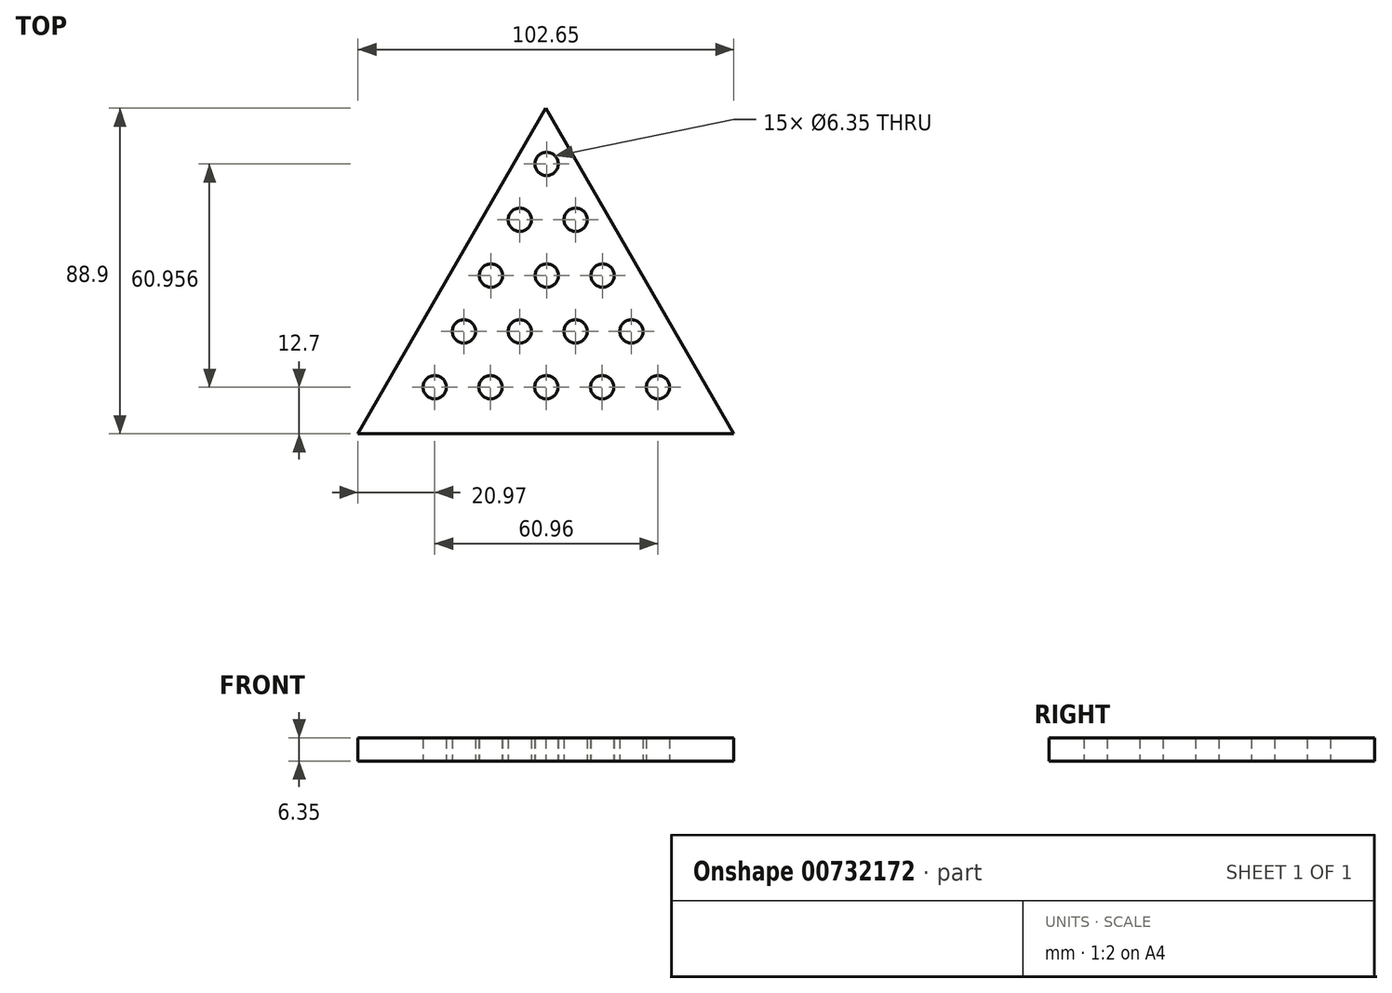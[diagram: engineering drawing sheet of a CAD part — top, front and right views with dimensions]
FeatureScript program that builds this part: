
annotation { "Feature Type Name" : "Feature", "Feature Type Description" : "" }
export const myFeature = defineFeature(function(context is Context, id is Id, definition is map)
    precondition{}
    {
        {
            var Q0;
            Q0=qCreatedBy(makeId("Top.planeOp"),FACE);
            var sketch = newSketch(context, id + "F0", { "sketchPlane" : qUnion([Q0])});
            skLineSegment(sketch, "E0.bottom", {"start": v(0, 0) * mm, "end": v(88.9, 0) * mm});
            skLineSegment(sketch, "E0.top", {"start": v(0, 88.9) * mm, "end": v(88.9, 88.9) * mm});
            skLineSegment(sketch, "E0.left", {"start": v(0, 0) * mm, "end": v(0, 88.9) * mm});
            skLineSegment(sketch, "E0.right", {"start": v(88.9, 0) * mm, "end": v(88.9, 88.9) * mm});
            skSolve(sketch);
        }
        {
            var Q0;
            Q0=makeQuery(id+"F0.imprint","IMPRINT",FACE,{"disambiguationData":[TD([[makeQuery(id+"F0.imprint","IMPRINT",EDGE,{"derivedFrom":sQuery(id+"F0.wireOp",EDGE,"E0.bottom")}),1.0]])]});
            var sketch = newSketch(context, id + "F1", { "sketchPlane" : qUnion([Q0])});
            skCircle(sketch, "E1", {"center": v(12.7, 12.7) * mm, "radius": 3.18 * mm});
            skCircle(sketch, "E2.1.0.0", {"center": v(27.94, 12.7) * mm, "radius": 3.18 * mm});
            skCircle(sketch, "E2.2.0.0", {"center": v(43.18, 12.7) * mm, "radius": 3.18 * mm});
            skCircle(sketch, "E2.3.0.0", {"center": v(58.42, 12.7) * mm, "radius": 3.18 * mm});
            skCircle(sketch, "E2.4.0.0", {"center": v(73.66, 12.7) * mm, "radius": 3.18 * mm});
            skLineSegment(sketch, "E2.direction1", {"start": v(12.7, 12.7) * mm, "end": v(27.94, 12.7) * mm, "construction": true});
            skSolve(sketch);
        }
        {
            var Q0;
            Q0=makeQuery(id+"F0.imprint","IMPRINT",FACE,{"disambiguationData":[TD([[makeQuery(id+"F0.imprint","IMPRINT",EDGE,{"derivedFrom":sQuery(id+"F0.wireOp",EDGE,"E0.bottom")}),1.0]])]});
            var sketch = newSketch(context, id + "F2", { "sketchPlane" : qUnion([Q0])});
            skCircle(sketch, "E3", {"center": v(20.67, 27.94) * mm, "radius": 3.18 * mm});
            skCircle(sketch, "E4.1.0.0", {"center": v(35.9, 27.94) * mm, "radius": 3.18 * mm});
            skCircle(sketch, "E4.2.0.0", {"center": v(51.15, 27.94) * mm, "radius": 3.18 * mm});
            skCircle(sketch, "E4.3.0.0", {"center": v(66.39, 27.94) * mm, "radius": 3.18 * mm});
            skLineSegment(sketch, "E4.direction1", {"start": v(20.67, 27.94) * mm, "end": v(35.9, 27.94) * mm, "construction": true});
            skSolve(sketch);
        }
        {
            var Q0;
            Q0=makeQuery(id+"F1.imprint","IMPRINT",FACE,{"disambiguationData":[TD([[makeQuery(id+"F1.imprint","IMPRINT",EDGE,{"derivedFrom":sQuery(id+"F1.wireOp",EDGE,"E1")}),-1.0]])]});
            var sketch = newSketch(context, id + "F3", { "sketchPlane" : qUnion([Q0])});
            skCircle(sketch, "E5", {"center": v(28.08, 43.18) * mm, "radius": 3.17 * mm});
            skCircle(sketch, "E6.1.0.0", {"center": v(43.32, 43.18) * mm, "radius": 3.17 * mm});
            skCircle(sketch, "E6.2.0.0", {"center": v(58.56, 43.18) * mm, "radius": 3.17 * mm});
            skLineSegment(sketch, "E6.direction1", {"start": v(28.08, 43.18) * mm, "end": v(43.32, 43.18) * mm, "construction": true});
            skSolve(sketch);
        }
        {
            var Q0;
            Q0=makeQuery(id+"F1.imprint","IMPRINT",FACE,{"disambiguationData":[TD([[makeQuery(id+"F1.imprint","IMPRINT",EDGE,{"derivedFrom":sQuery(id+"F1.wireOp",EDGE,"E1")}),-1.0]])]});
            var sketch = newSketch(context, id + "F4", { "sketchPlane" : qUnion([Q0])});
            skCircle(sketch, "E7", {"center": v(35.94, 58.42) * mm, "radius": 3.18 * mm});
            skCircle(sketch, "E8.1.0.0", {"center": v(51.18, 58.42) * mm, "radius": 3.18 * mm});
            skLineSegment(sketch, "E8.direction1", {"start": v(35.94, 58.42) * mm, "end": v(51.18, 58.42) * mm, "construction": true});
            skSolve(sketch);
        }
        {
            var Q0;
            Q0=makeQuery(id+"F2.imprint","IMPRINT",FACE,{"disambiguationData":[TD([[makeQuery(id+"F2.imprint","IMPRINT",EDGE,{"derivedFrom":sQuery(id+"F2.wireOp",EDGE,"E3")}),-1.0]])]});
            var sketch = newSketch(context, id + "F5", { "sketchPlane" : qUnion([Q0])});
            skCircle(sketch, "E9", {"center": v(43.23, 73.66) * mm, "radius": 3.17 * mm});
            skSolve(sketch);
        }
        {
            var Q0;
            Q0=makeQuery(id+"F1.imprint","IMPRINT",FACE,{"disambiguationData":[TD([[makeQuery(id+"F1.imprint","IMPRINT",EDGE,{"derivedFrom":sQuery(id+"F1.wireOp",EDGE,"E1")}),-1.0]])]});
            var sketch = newSketch(context, id + "F6", { "sketchPlane" : qUnion([Q0])});
            skCircle(sketch, "E10.cCircle", {"center": v(43.05, 29.63) * mm, "radius": 29.63 * mm, "construction": true});
            skLineSegment(sketch, "E10.0", {"start": v(94.38, 0) * mm, "end": v(-8.27, 0) * mm});
            skLineSegment(sketch, "E10.1", {"start": v(-8.27, 0) * mm, "end": v(43.05, 88.9) * mm});
            skLineSegment(sketch, "E10.2", {"start": v(43.05, 88.9) * mm, "end": v(94.38, 0) * mm});
            skPoint(sketch, "E10.0.midPoint", {"position": v(43.05, 0) * mm});
            skSolve(sketch);
        }
        {
            var Q0;
            Q0 = qSketchRegion(id + "F6", true);
            extrude(context, id + "F7", {"entities" : qUnion([Q0]), "depth" : 6.35 * mm, "offsetDistance" : 25.4 * mm});
        }
        {
            var Q0;
            Q0 = qSketchRegion(id + "F5", true);
            var Q1;
            Q1 = qSketchRegion(id + "F1", true);
            var Q2;
            Q2 = qSketchRegion(id + "F2", true);
            var Q3;
            Q3 = qSketchRegion(id + "F3", true);
            var Q4;
            Q4 = qSketchRegion(id + "F4", true);
            extrude(context, id + "F8", {"entities" : qUnion([Q0, Q1, Q2, Q3, Q4]), "operationType" : NewBodyOperationType.REMOVE, "endBound" : BoundingType.UP_TO_NEXT, "depth" : 25.4 * mm, "offsetDistance" : 25.4 * mm});
        }
    });
